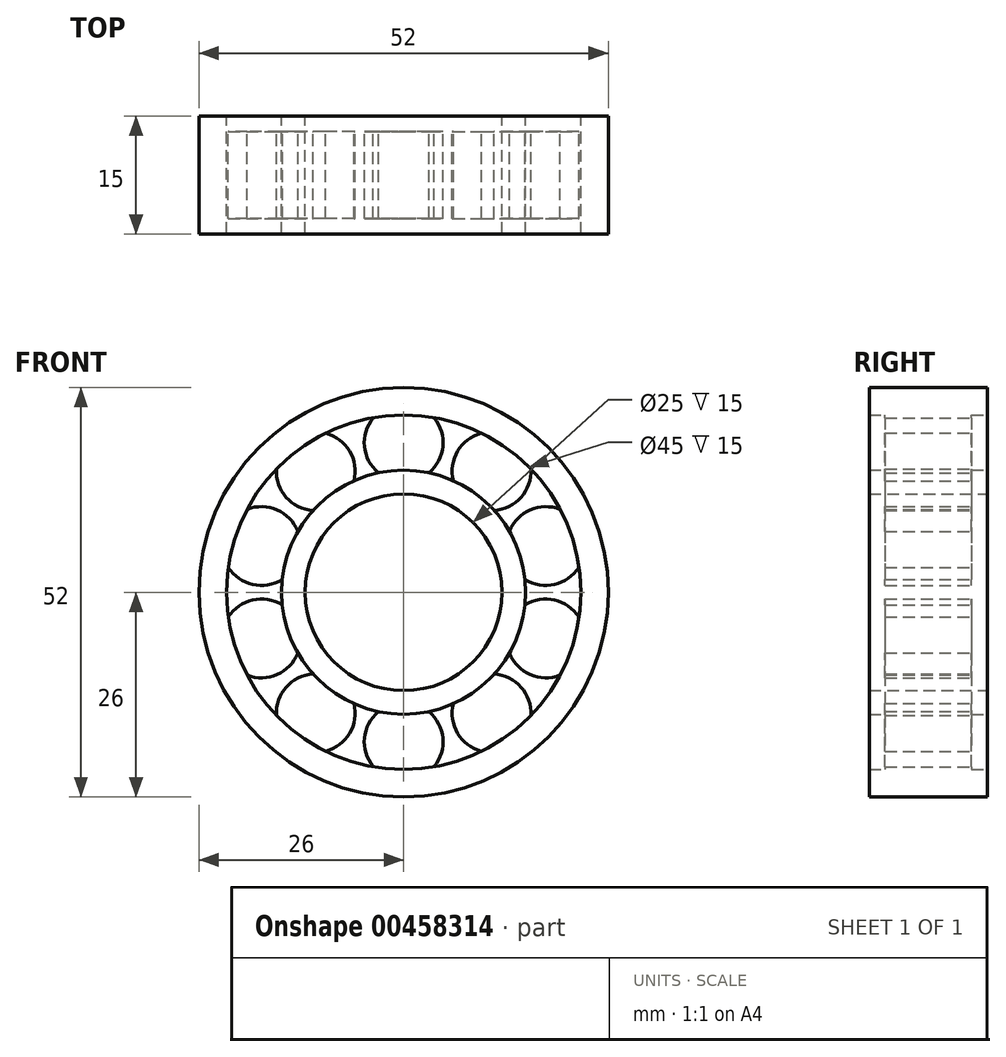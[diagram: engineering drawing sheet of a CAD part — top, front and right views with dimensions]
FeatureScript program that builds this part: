
annotation { "Feature Type Name" : "Feature", "Feature Type Description" : "" }
export const myFeature = defineFeature(function(context is Context, id is Id, definition is map)
    precondition{}
    {
        {
            var Q0;
            Q0=qCreatedBy(makeId("Front.planeOp"),FACE);
            cPlane(context, id + "F0", {"entities" : qUnion([Q0]), "cplaneType" : CPlaneType.OFFSET, "offset" : 7.5 * mm, "width" : 150 * mm, "height" : 150 * mm});
        }
        {
            var Q0;
            Q0=qCreatedBy(makeId("Front.planeOp"),FACE);
            var sketch = newSketch(context, id + "F1", { "sketchPlane" : qUnion([Q0])});
            skCircle(sketch, "E0", {"center": v(0, 0) * mm, "radius": 22.5 * mm});
            skCircle(sketch, "E1", {"center": v(0, 0) * mm, "radius": 26 * mm});
            skSolve(sketch);
        }
        {
            var Q0;
            Q0=qCreatedBy(makeId("Front.planeOp"),FACE);
            var sketch = newSketch(context, id + "F2", { "sketchPlane" : qUnion([Q0])});
            skCircle(sketch, "E2", {"center": v(0, 0) * mm, "radius": 12.5 * mm});
            skCircle(sketch, "E3", {"center": v(0, 0) * mm, "radius": 15.5 * mm});
            skSolve(sketch);
        }
        {
            var Q0;
            Q0=qCreatedBy(id+"F0.planeOp",FACE);
            var sketch = newSketch(context, id + "F3", { "sketchPlane" : qUnion([Q0])});
            skCircle(sketch, "E4", {"center": v(0, 19) * mm, "radius": 5 * mm});
            skCircle(sketch, "E5.1.0", {"center": v(-11.17, 15.37) * mm, "radius": 5 * mm});
            skCircle(sketch, "E5.2.0", {"center": v(-18.07, 5.87) * mm, "radius": 5 * mm});
            skCircle(sketch, "E5.3.0", {"center": v(-18.07, -5.87) * mm, "radius": 5 * mm});
            skCircle(sketch, "E5.4.0", {"center": v(-11.17, -15.37) * mm, "radius": 5 * mm});
            skCircle(sketch, "E5.5.0", {"center": v(0, -19) * mm, "radius": 5 * mm});
            skCircle(sketch, "E5.6.0", {"center": v(11.17, -15.37) * mm, "radius": 5 * mm});
            skCircle(sketch, "E5.7.0", {"center": v(18.07, -5.87) * mm, "radius": 5 * mm});
            skCircle(sketch, "E5.8.0", {"center": v(18.07, 5.87) * mm, "radius": 5 * mm});
            skCircle(sketch, "E5.9.0", {"center": v(11.17, 15.37) * mm, "radius": 5 * mm});
            skPoint(sketch, "E5.center", {"position": v(0, 0) * mm});
            skSolve(sketch);
        }
        {
            var Q0;
            Q0 = qSketchRegion(id + "F2", true);
            extrude(context, id + "F4", {"entities" : qUnion([Q0]), "depth" : 15 * mm, "offsetDistance" : 25 * mm});
        }
        {
            var Q0;
            Q0 = qSketchRegion(id + "F3", true);
            extrude(context, id + "F5", {"entities" : qUnion([Q0]), "operationType" : NewBodyOperationType.ADD, "depth" : 11 * mm, "offsetDistance" : 25 * mm, "symmetric" : true});
        }
        {
            var Q0;
            Q0 = qSketchRegion(id + "F1", true);
            extrude(context, id + "F6", {"entities" : qUnion([Q0]), "operationType" : NewBodyOperationType.ADD, "depth" : 15 * mm, "offsetDistance" : 25 * mm});
        }
    });
